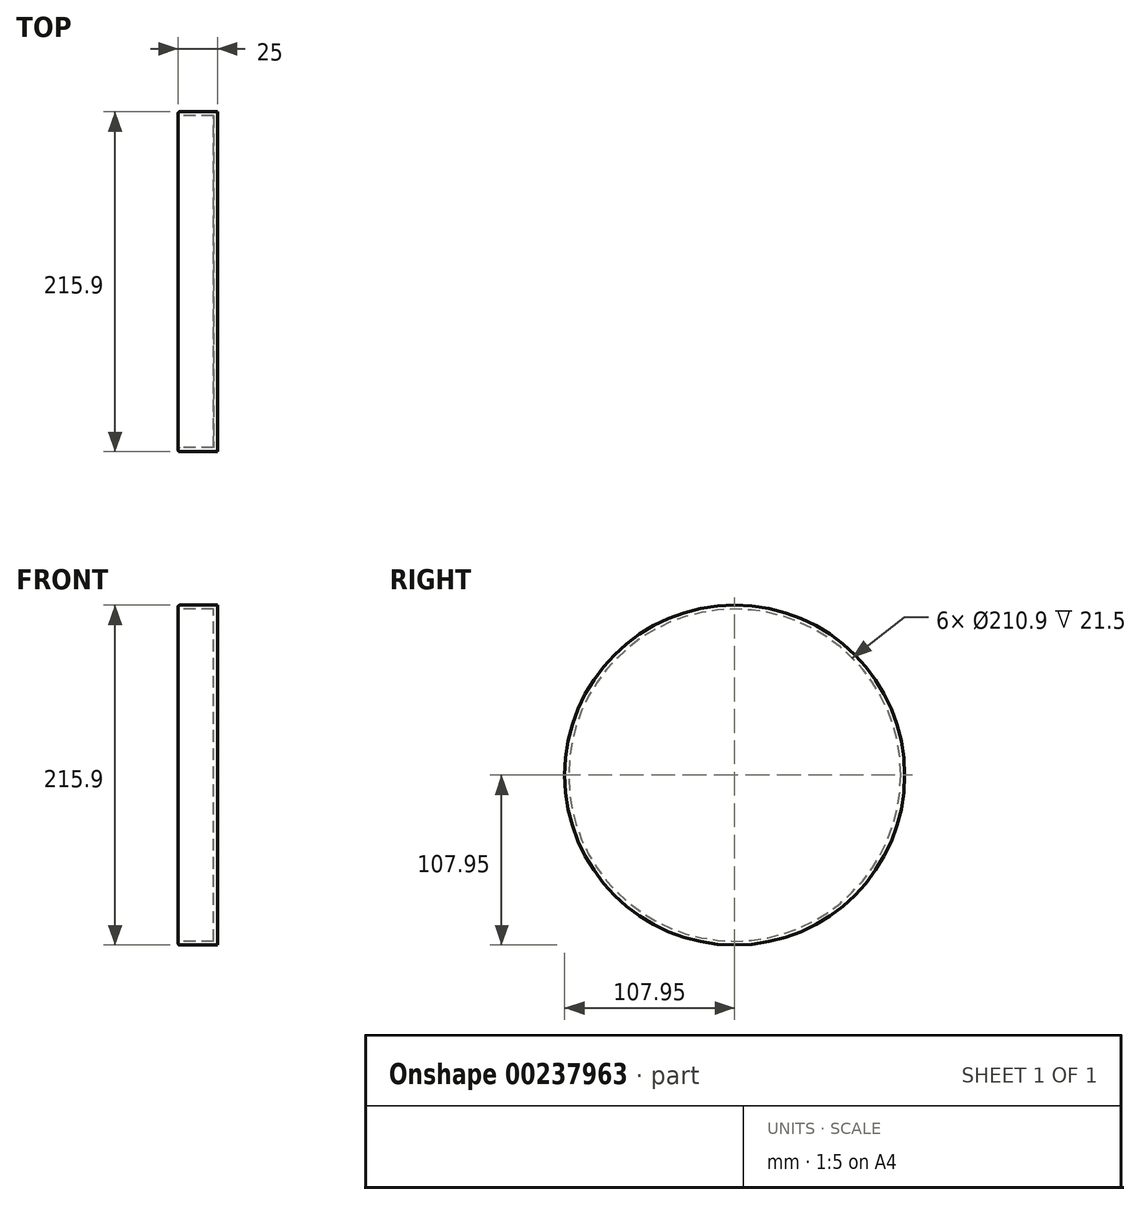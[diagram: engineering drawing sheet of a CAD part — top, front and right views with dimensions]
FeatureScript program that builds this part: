
annotation { "Feature Type Name" : "Feature", "Feature Type Description" : "" }
export const myFeature = defineFeature(function(context is Context, id is Id, definition is map)
    precondition{}
    {
        {
            var Q0;
            Q0=qCreatedBy(makeId("Right.planeOp"),FACE);
            var sketch = newSketch(context, id + "F0", { "sketchPlane" : qUnion([Q0])});
            skCircle(sketch, "E0", {"center": v(0, 0) * mm, "radius": 107.95 * mm});
            skSolve(sketch);
        }
        {
            var Q0;
            Q0=makeQuery(id+"F0.imprint","IMPRINT",FACE,{"disambiguationData":[TD([[makeQuery(id+"F0.imprint","IMPRINT",EDGE,{"derivedFrom":sQuery(id+"F0.wireOp",EDGE,"E0")}),1.0]])]});
            extrude(context, id + "F1", {"entities" : qUnion([Q0]), "depth" : 25 * mm});
        }
        {
            var Q0;
            Q0=makeQuery(id+"F1.opExtrude","CAP_FACE",FACE,{"disambiguationData":[OSD([sQuery(id+"F0.wireOp",EDGE,"E0")])],"isStart":true});
            shell(context, id + "F2", {"entities" : qUnion([Q0]), "thickness" : 2.5 * mm});
        }
        {
            var Q0;
            Q0=makeQuery(id+"F1.opExtrude","CAP_EDGE",EDGE,{"disambiguationData":[OSD([sQuery(id+"F0.wireOp",EDGE,"E0")])],"isStart":true});
            var Q1;
            {var subQ0=sQuery(id+"F0.wireOp",EDGE,"E0");Q1=makeQuery(id+"F2.opShell","OFFSET_EDGE",EDGE,{"disambiguationData":[OSD([subQ0]),TDD([makeQuery(id+"F1.opExtrude","CAP_EDGE",EDGE,{"disambiguationData":[OSD([subQ0])],"isStart":true})])]});}
            fillet(context, id + "F3", {"entities" : qUnion([Q0, Q1]), "radius" : 1 * mm, "tangentPropagation" : true, "allowEdgeOverflow" : false});
        }
    });
